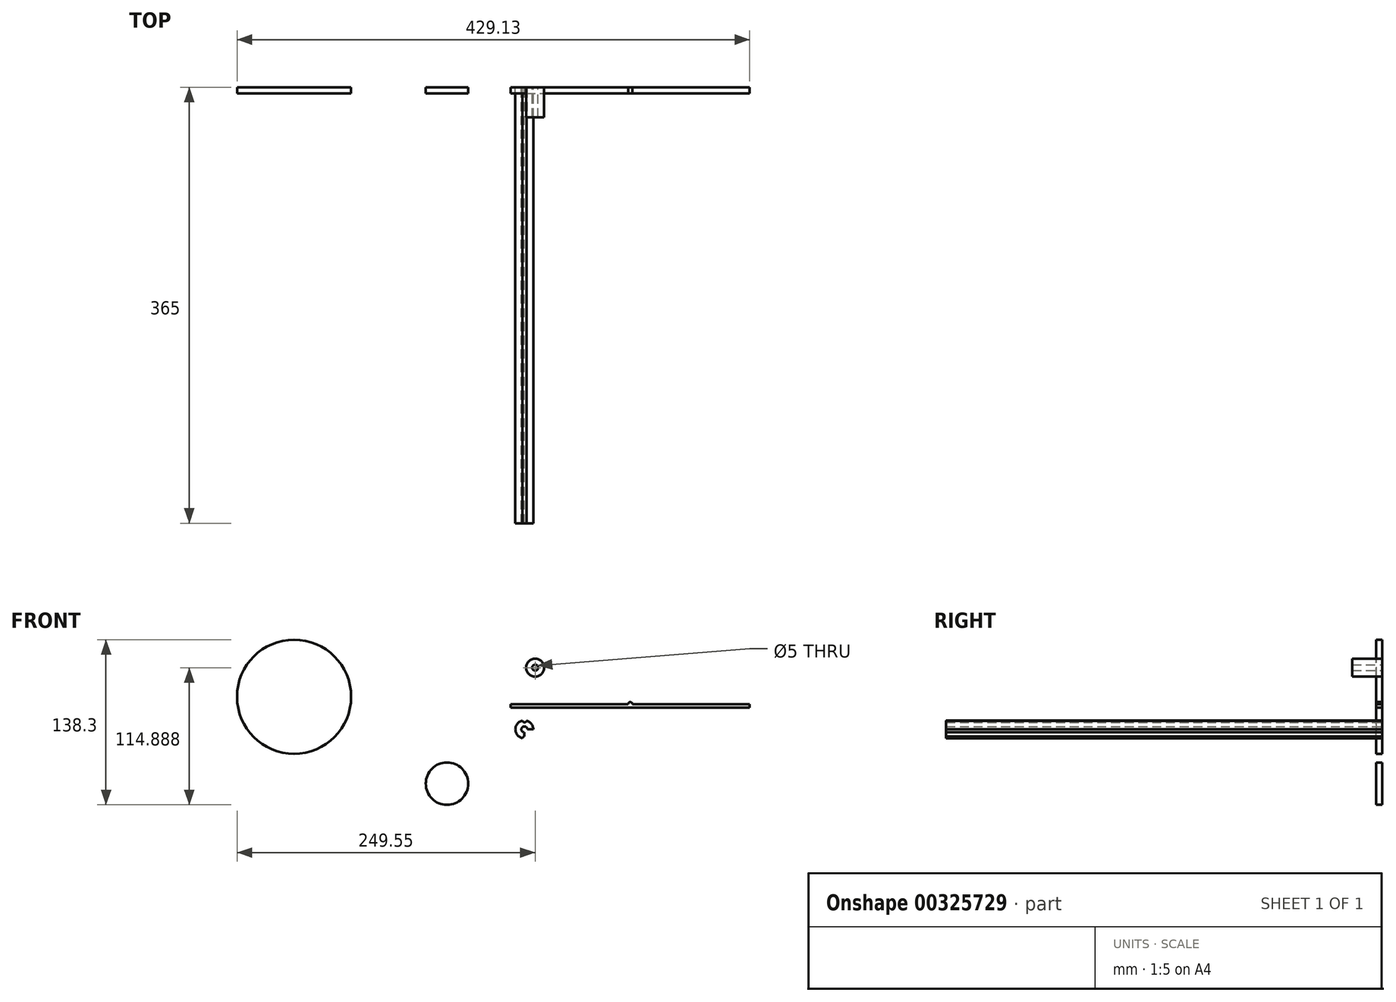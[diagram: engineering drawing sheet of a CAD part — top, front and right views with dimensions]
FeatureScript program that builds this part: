
annotation { "Feature Type Name" : "Feature", "Feature Type Description" : "" }
export const myFeature = defineFeature(function(context is Context, id is Id, definition is map)
    precondition{}
    {
        {
            var Q0;
            Q0=qCreatedBy(makeId("Front.planeOp"),FACE);
            var sketch = newSketch(context, id + "F0", { "sketchPlane" : qUnion([Q0])});
            skCircle(sketch, "E0", {"center": v(-39.07, 51.72) * mm, "radius": 7.5 * mm});
            skLineSegment(sketch, "E1.bottom", {"start": v(54.63, -36.21) * mm, "end": v(53.7, -36.21) * mm});
            skLineSegment(sketch, "E1.top", {"start": v(54.63, -146.89) * mm, "end": v(53.7, -146.89) * mm});
            skLineSegment(sketch, "E1.left", {"start": v(54.63, -36.21) * mm, "end": v(54.63, -146.89) * mm});
            skLineSegment(sketch, "E1.right", {"start": v(53.7, -36.21) * mm, "end": v(53.7, -146.89) * mm});
            skPoint(sketch, "E1.middle", {"position": v(54.17, -91.55) * mm});
            skLineSegment(sketch, "E2", {"start": v(-55.63, 0) * mm, "end": v(-40.63, 0) * mm});
            skPoint(sketch, "E3", {"position": v(-48.13, 0) * mm});
            skLineSegment(sketch, "E4", {"start": v(-48.13, 0) * mm, "end": v(-48.13, 7.5) * mm});
            skLineSegment(sketch, "E5", {"start": v(-57.11, 7.5) * mm, "end": v(-29.98, 7.5) * mm, "construction": true});
            skArc(sketch, "E6", {"start": v(-49.76, 7.5) * mm, "mid": v(-47.92, 5.94) * mm, "end": v(-46.08, 7.5) * mm});
            skArc(sketch, "E7", {"start": v(-55.63, 0) * mm, "mid": v(-53.97, 4.7) * mm, "end": v(-49.72, 7.33) * mm});
            skArc(sketch, "E8", {"start": v(-40.63, 0) * mm, "mid": v(-42.17, 4.55) * mm, "end": v(-46.15, 7.23) * mm});
            skLineSegment(sketch, "E9", {"start": v(-65.26, 0) * mm, "end": v(-27.4, 0) * mm, "construction": true});
            skArc(sketch, "E10.MirrorCS", {"start": v(-40.63, 0) * mm, "mid": v(-42.3, 4.7) * mm, "end": v(-46.54, 7.33) * mm});
            skLineSegment(sketch, "E11.MirrorCS", {"start": v(-48.13, 0) * mm, "end": v(-48.13, -7.5) * mm});
            skArc(sketch, "E12.MirrorCS", {"start": v(-55.63, 0) * mm, "mid": v(-53.97, -4.7) * mm, "end": v(-49.72, -7.33) * mm});
            skArc(sketch, "E13.MirrorCS", {"start": v(-40.63, 0) * mm, "mid": v(-42.17, -4.55) * mm, "end": v(-46.15, -7.23) * mm});
            skArc(sketch, "E14.MirrorCS", {"start": v(-49.76, -7.5) * mm, "mid": v(-47.92, -5.94) * mm, "end": v(-46.08, -7.5) * mm});
            skCircle(sketch, "E15", {"center": v(40.51, 21.06) * mm, "radius": 1.82 * mm});
            skPoint(sketch, "E16", {"position": v(140.51, 21.06) * mm});
            skPoint(sketch, "E17", {"position": v(-59.49, 21.06) * mm});
            skLineSegment(sketch, "E18", {"start": v(-59.49, 21.06) * mm, "end": v(40.51, 21.06) * mm});
            skLineSegment(sketch, "E19", {"start": v(140.51, 21.06) * mm, "end": v(40.51, 21.06) * mm});
            skPoint(sketch, "E20", {"position": v(-59.49, 18.34) * mm});
            skPoint(sketch, "E21", {"position": v(140.51, 18.34) * mm});
            skLineSegment(sketch, "E22", {"start": v(-59.49, 21.06) * mm, "end": v(-59.49, 18.34) * mm});
            skLineSegment(sketch, "E23", {"start": v(140.51, 21.06) * mm, "end": v(140.51, 18.34) * mm});
            skLineSegment(sketch, "E24", {"start": v(-59.49, 18.34) * mm, "end": v(140.51, 18.34) * mm});
            skCircle(sketch, "E25", {"center": v(-112.88, -45.42) * mm, "radius": 17.75 * mm});
            skCircle(sketch, "E26", {"center": v(-240.87, 27.38) * mm, "radius": 47.75 * mm});
            skSolve(sketch);
        }
        {
            var Q0;
            {var subQ0=sQuery(id+"F0.wireOp",EDGE,"E7");Q0=makeQuery(id+"F0.imprint","IMPRINT",FACE,{"disambiguationData":[TD([[makeQuery(id+"F0.imprint","IMPRINT",EDGE,{"derivedFrom":subQ0}),-1.0]])]});}
            var Q1;
            {var subQ0=sQuery(id+"F0.wireOp",EDGE,"E10.MirrorCS");var subQ5=sQuery(id+"F0.wireOp",EDGE,"E6");var subQ6=makeQuery(id+"F0.imprint","INTERSECT",VERTEX,{"derivedFrom":[subQ5,subQ0]});Q1=makeQuery(id+"F0.imprint","IMPRINT",FACE,{"disambiguationData":[TD([[makeQuery(id+"F0.imprint","IMPRINT",EDGE,{"disambiguationData":[TD([[subQ6,1.0]])],"derivedFrom":subQ5}),-1.0]])]});}
            var Q2;
            {var subQ0=sQuery(id+"F0.wireOp",EDGE,"E13.MirrorCS");Q2=makeQuery(id+"F0.imprint","IMPRINT",FACE,{"disambiguationData":[TD([[makeQuery(id+"F0.imprint","IMPRINT",EDGE,{"derivedFrom":subQ0}),-1.0]])]});}
            var Q3;
            {var subQ0=sQuery(id+"F0.wireOp",EDGE,"E12.MirrorCS");Q3=makeQuery(id+"F0.imprint","IMPRINT",FACE,{"disambiguationData":[TD([[makeQuery(id+"F0.imprint","IMPRINT",EDGE,{"derivedFrom":subQ0}),1.0]])]});}
            extrude(context, id + "F1", {"entities" : qUnion([Q0, Q1, Q2, Q3]), "depth" : 365 * mm});
        }
        {
            var Q0;
            Q0=sQuery(id+"F0.wireOp",VERTEX,"E3");
            var Q1;
            Q1=makeQuery(id+"F1.opExtrude","SWEPT_BODY",BODY,{"disambiguationData":[OSD([sQuery(id+"F0.wireOp",EDGE,"E6"),sQuery(id+"F0.wireOp",EDGE,"E7"),sQuery(id+"F0.wireOp",EDGE,"E10.MirrorCS"),sQuery(id+"F0.wireOp",EDGE,"E12.MirrorCS"),sQuery(id+"F0.wireOp",EDGE,"E13.MirrorCS"),sQuery(id+"F0.wireOp",EDGE,"E14.MirrorCS")])]});
            hole(context, id + "F2", {"style" : HoleStyle.SIMPLE, "endStyle" : HoleEndStyle.THROUGH, "oppositeDirection" : true, "holeDiameter" : 5 * mm, "tappedDepth" : 12 * mm, "tapClearance" : 3, "locations" : qUnion([Q0]), "scope" : qUnion([Q1])});
        }
        {
            var Q0;
            Q0=makeQuery(id+"F0.imprint","IMPRINT",FACE,{"disambiguationData":[TD([[makeQuery(id+"F0.imprint","IMPRINT",EDGE,{"derivedFrom":sQuery(id+"F0.wireOp",EDGE,"E0")}),1.0]])]});
            extrude(context, id + "F3", {"entities" : qUnion([Q0]), "depth" : 25 * mm});
        }
        {
            var Q0;
            Q0=sQuery(id+"F0.wireOp",VERTEX,"E0.center");
            var Q1;
            Q1=makeQuery(id+"F3.opExtrude","SWEPT_BODY",BODY,{"disambiguationData":[OSD([sQuery(id+"F0.wireOp",EDGE,"E0")])]});
            hole(context, id + "F4", {"style" : HoleStyle.SIMPLE, "endStyle" : HoleEndStyle.THROUGH, "oppositeDirection" : true, "holeDiameter" : 5 * mm, "tappedDepth" : 12 * mm, "tapClearance" : 3, "locations" : qUnion([Q0]), "scope" : qUnion([Q1])});
        }
        {
            var Q0;
            {var subQ4=sQuery(id+"F0.wireOp",EDGE,"E22");Q0=makeQuery(id+"F0.imprint","IMPRINT",FACE,{"disambiguationData":[TD([[makeQuery(id+"F0.imprint","IMPRINT",EDGE,{"derivedFrom":subQ4}),1.0]])]});}
            var Q1;
            {var subQ0=sQuery(id+"F0.wireOp",EDGE,"E18");var subQ1=sQuery(id+"F0.wireOp",EDGE,"E15");var subQ2=makeQuery(id+"F0.imprint","INTERSECT",VERTEX,{"derivedFrom":[subQ1,subQ0]});Q1=makeQuery(id+"F0.imprint","IMPRINT",FACE,{"disambiguationData":[TD([[makeQuery(id+"F0.imprint","IMPRINT",EDGE,{"disambiguationData":[TD([[subQ2,1.0]])],"derivedFrom":subQ1}),1.0]])]});}
            var Q2;
            {var subQ0=sQuery(id+"F0.wireOp",EDGE,"E18");var subQ1=sQuery(id+"F0.wireOp",EDGE,"E15");var subQ2=makeQuery(id+"F0.imprint","INTERSECT",VERTEX,{"derivedFrom":[subQ1,subQ0]});Q2=makeQuery(id+"F0.imprint","IMPRINT",FACE,{"disambiguationData":[TD([[makeQuery(id+"F0.imprint","IMPRINT",EDGE,{"disambiguationData":[TD([[subQ2,-1.0]])],"derivedFrom":subQ1}),1.0]])]});}
            extrude(context, id + "F5", {"entities" : qUnion([Q0, Q1, Q2]), "depth" : 5 * mm});
        }
        {
            var Q0;
            Q0=makeQuery(id+"F0.imprint","IMPRINT",FACE,{"disambiguationData":[TD([[makeQuery(id+"F0.imprint","IMPRINT",EDGE,{"derivedFrom":sQuery(id+"F0.wireOp",EDGE,"E25")}),1.0]])]});
            var Q1;
            Q1=makeQuery(id+"F0.imprint","IMPRINT",FACE,{"disambiguationData":[TD([[makeQuery(id+"F0.imprint","IMPRINT",EDGE,{"derivedFrom":sQuery(id+"F0.wireOp",EDGE,"E26")}),1.0]])]});
            extrude(context, id + "F6", {"entities" : qUnion([Q0, Q1]), "depth" : 5 * mm});
        }
    });
